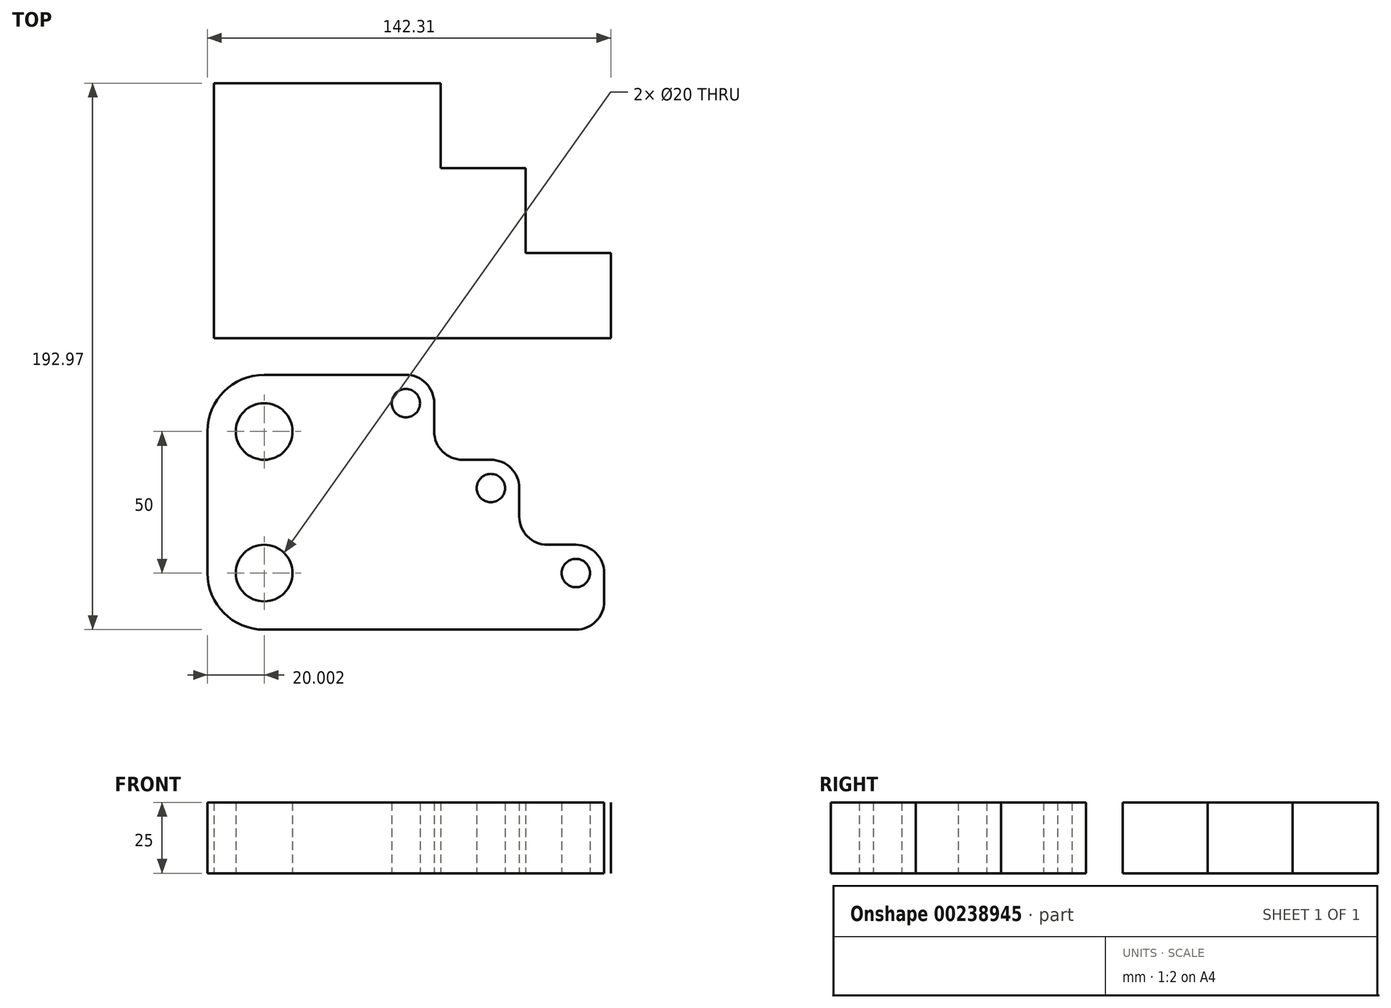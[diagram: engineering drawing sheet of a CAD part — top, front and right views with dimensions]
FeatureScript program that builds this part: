
annotation { "Feature Type Name" : "Feature", "Feature Type Description" : "" }
export const myFeature = defineFeature(function(context is Context, id is Id, definition is map)
    precondition{}
    {
        {
            var Q0;
            Q0=qCreatedBy(makeId("Top.planeOp"),FACE);
            var sketch = newSketch(context, id + "F0", { "sketchPlane" : qUnion([Q0])});
            skLineSegment(sketch, "E0", {"start": v(-52.44, -69.36) * mm, "end": v(57.56, -69.36) * mm});
            skLineSegment(sketch, "E1", {"start": v(-72.44, -49.36) * mm, "end": v(-72.44, 0.64) * mm});
            skLineSegment(sketch, "E2", {"start": v(67.56, -59.36) * mm, "end": v(67.56, -49.36) * mm});
            skLineSegment(sketch, "E3", {"start": v(57.56, -39.36) * mm, "end": v(47.56, -39.36) * mm});
            skLineSegment(sketch, "E4", {"start": v(37.56, -29.36) * mm, "end": v(37.56, -19.36) * mm});
            skLineSegment(sketch, "E5", {"start": v(27.56, -9.36) * mm, "end": v(17.56, -9.36) * mm});
            skLineSegment(sketch, "E6", {"start": v(7.56, 0.64) * mm, "end": v(7.56, 10.64) * mm});
            skLineSegment(sketch, "E7", {"start": v(-2.44, 20.64) * mm, "end": v(-52.44, 20.64) * mm});
            skPoint(sketch, "E8.visualSharp", {"position": v(-72.44, 20.64) * mm});
            skArc(sketch, "E8.filletArc", {"start": v(-52.44, 20.64) * mm, "mid": v(-66.58, 14.78) * mm, "end": v(-72.44, 0.64) * mm});
            skPoint(sketch, "E9.visualSharp", {"position": v(-72.44, -69.36) * mm});
            skArc(sketch, "E9.filletArc", {"start": v(-72.44, -49.36) * mm, "mid": v(-66.58, -63.5) * mm, "end": v(-52.44, -69.36) * mm});
            skPoint(sketch, "E10.visualSharp", {"position": v(67.56, -69.36) * mm});
            skArc(sketch, "E10.filletArc", {"start": v(57.56, -69.36) * mm, "mid": v(64.63, -66.43) * mm, "end": v(67.56, -59.36) * mm});
            skPoint(sketch, "E11.visualSharp", {"position": v(67.56, -39.36) * mm});
            skArc(sketch, "E11.filletArc", {"start": v(67.56, -49.36) * mm, "mid": v(64.63, -42.3) * mm, "end": v(57.56, -39.36) * mm});
            skPoint(sketch, "E12.visualSharp", {"position": v(37.56, -39.36) * mm});
            skArc(sketch, "E12.filletArc", {"start": v(37.56, -29.36) * mm, "mid": v(40.5, -36.43) * mm, "end": v(47.56, -39.36) * mm});
            skPoint(sketch, "E13.visualSharp", {"position": v(37.56, -9.36) * mm});
            skArc(sketch, "E13.filletArc", {"start": v(37.56, -19.36) * mm, "mid": v(34.63, -12.3) * mm, "end": v(27.56, -9.36) * mm});
            skPoint(sketch, "E14.visualSharp", {"position": v(7.56, -9.36) * mm});
            skArc(sketch, "E14.filletArc", {"start": v(7.56, 0.64) * mm, "mid": v(10.5, -6.43) * mm, "end": v(17.56, -9.36) * mm});
            skPoint(sketch, "E15.visualSharp", {"position": v(7.56, 20.64) * mm});
            skArc(sketch, "E15.filletArc", {"start": v(7.56, 10.64) * mm, "mid": v(4.63, 17.7) * mm, "end": v(-2.44, 20.64) * mm});
            skCircle(sketch, "E16", {"center": v(-52.44, -49.36) * mm, "radius": 10 * mm});
            skCircle(sketch, "E17", {"center": v(-52.44, 0.64) * mm, "radius": 10 * mm});
            skCircle(sketch, "E18", {"center": v(-2.44, 10.64) * mm, "radius": 5 * mm});
            skCircle(sketch, "E19", {"center": v(27.56, -19.36) * mm, "radius": 5 * mm});
            skCircle(sketch, "E20", {"center": v(57.56, -49.36) * mm, "radius": 5 * mm});
            skLineSegment(sketch, "E21", {"start": v(-70.13, 33.61) * mm, "end": v(69.87, 33.61) * mm});
            skLineSegment(sketch, "E22", {"start": v(69.87, 33.61) * mm, "end": v(-70.13, 33.61) * mm});
            skLineSegment(sketch, "E23", {"start": v(-70.13, 33.61) * mm, "end": v(-70.13, 123.61) * mm});
            skLineSegment(sketch, "E24", {"start": v(69.87, 33.61) * mm, "end": v(69.87, 63.61) * mm});
            skLineSegment(sketch, "E25", {"start": v(69.87, 63.61) * mm, "end": v(39.87, 63.61) * mm});
            skLineSegment(sketch, "E26", {"start": v(39.87, 63.61) * mm, "end": v(39.87, 93.61) * mm});
            skLineSegment(sketch, "E27", {"start": v(39.87, 93.61) * mm, "end": v(9.87, 93.61) * mm});
            skLineSegment(sketch, "E28", {"start": v(9.87, 93.61) * mm, "end": v(9.87, 123.61) * mm});
            skLineSegment(sketch, "E29", {"start": v(9.87, 123.61) * mm, "end": v(-70.13, 123.61) * mm});
            skSolve(sketch);
        }
        {
            var Q0;
            Q0 = qSketchRegion(id + "F0", true);
            extrude(context, id + "F1", {"entities" : qUnion([Q0]), "depth" : 25 * mm});
        }
    });
